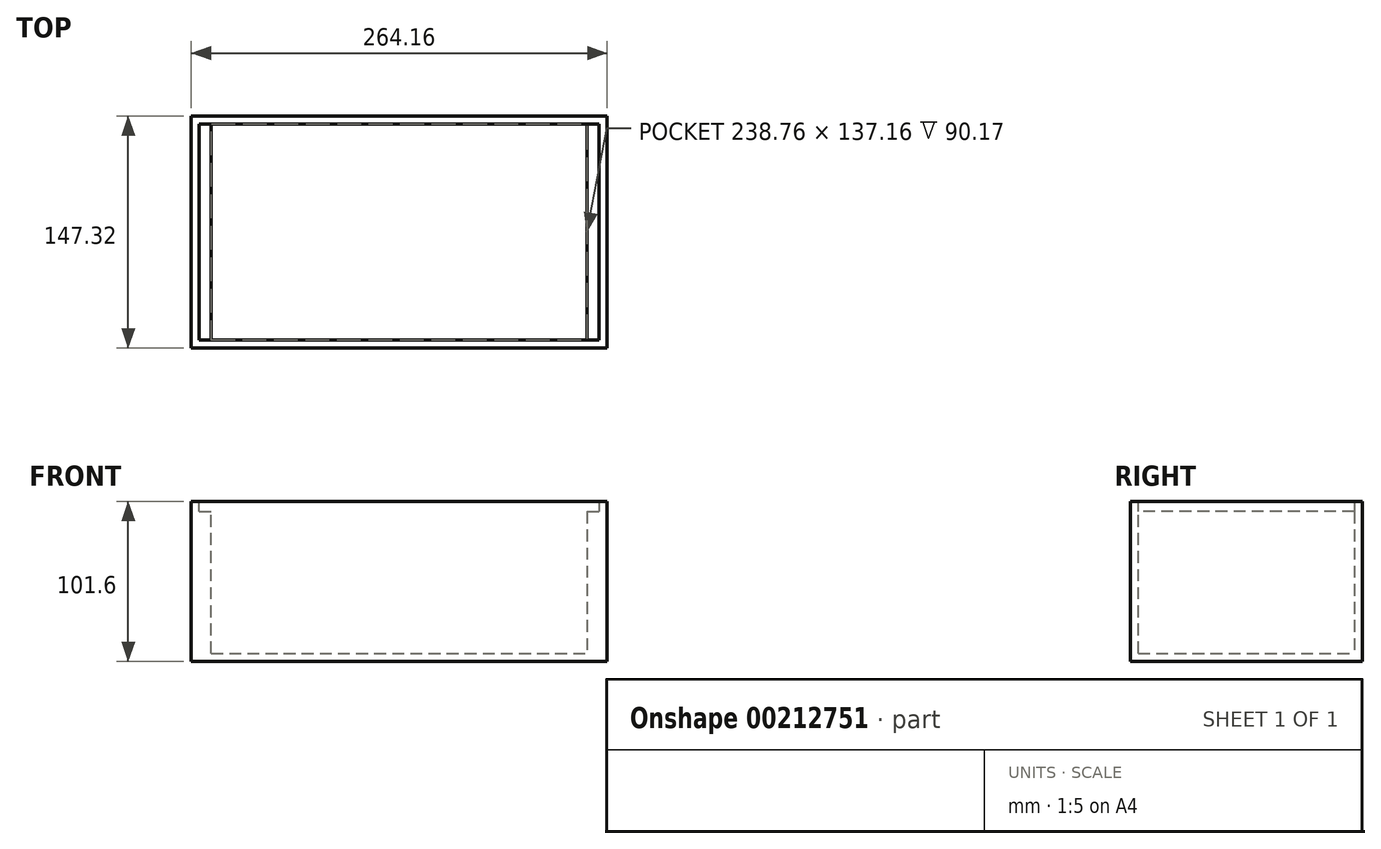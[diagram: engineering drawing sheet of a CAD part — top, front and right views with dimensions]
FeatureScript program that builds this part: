
annotation { "Feature Type Name" : "Feature", "Feature Type Description" : "" }
export const myFeature = defineFeature(function(context is Context, id is Id, definition is map)
    precondition{}
    {
        {
            var Q0;
            Q0=qCreatedBy(makeId("Top.planeOp"),FACE);
            var sketch = newSketch(context, id + "F0", { "sketchPlane" : qUnion([Q0])});
            skLineSegment(sketch, "E0.bottom", {"start": v(-132.08, 73.66) * mm, "end": v(132.08, 73.66) * mm});
            skLineSegment(sketch, "E0.top", {"start": v(-132.08, -73.66) * mm, "end": v(132.08, -73.66) * mm});
            skLineSegment(sketch, "E0.left", {"start": v(-132.08, 73.66) * mm, "end": v(-132.08, -73.66) * mm});
            skLineSegment(sketch, "E0.right", {"start": v(132.08, 73.66) * mm, "end": v(132.08, -73.66) * mm});
            skPoint(sketch, "E0.middle", {"position": v(0, 0) * mm});
            skSolve(sketch);
        }
        {
            var Q0;
            Q0=makeQuery(id+"F0.imprint","IMPRINT",FACE,{"disambiguationData":[TD([[makeQuery(id+"F0.imprint","IMPRINT",EDGE,{"derivedFrom":sQuery(id+"F0.wireOp",EDGE,"E0.bottom")}),-1.0]])]});
            extrude(context, id + "F1", {"entities" : qUnion([Q0]), "depth" : 5.08 * mm});
        }
        {
            var Q0;
            Q0=qCreatedBy(makeId("Right.planeOp"),FACE);
            cPlane(context, id + "F2", {"entities" : qUnion([Q0]), "cplaneType" : CPlaneType.OFFSET, "offset" : 132.08 * mm, "oppositeDirection" : true, "width" : 152.4 * mm, "height" : 152.4 * mm});
        }
        {
            var Q0;
            Q0=qCreatedBy(id+"F2.planeOp",FACE);
            var sketch = newSketch(context, id + "F3", { "sketchPlane" : qUnion([Q0])});
            skLineSegment(sketch, "E1", {"start": v(0, 0) * mm, "end": v(73.66, 0) * mm});
            skLineSegment(sketch, "E2", {"start": v(73.66, 0) * mm, "end": v(73.66, 95.25) * mm});
            skLineSegment(sketch, "E3", {"start": v(73.66, 95.25) * mm, "end": v(0, 95.25) * mm});
            skLineSegment(sketch, "E4.MirrorCS", {"start": v(-73.66, 95.25) * mm, "end": v(0, 95.25) * mm});
            skLineSegment(sketch, "E5.MirrorCS", {"start": v(-73.66, 0) * mm, "end": v(-73.66, 95.25) * mm});
            skLineSegment(sketch, "E6.MirrorCS", {"start": v(0, 0) * mm, "end": v(-73.66, 0) * mm});
            skSolve(sketch);
        }
        {
            var Q0;
            Q0=makeQuery(id+"F3.imprint","IMPRINT",FACE,{"disambiguationData":[TD([[makeQuery(id+"F3.imprint","IMPRINT",EDGE,{"derivedFrom":sQuery(id+"F3.wireOp",EDGE,"E1")}),1.0]])]});
            extrude(context, id + "F4", {"entities" : qUnion([Q0]), "depth" : 12.7 * mm});
        }
        {
            var Q0;
            Q0=qCreatedBy(makeId("Front.planeOp"),FACE);
            cPlane(context, id + "F5", {"entities" : qUnion([Q0]), "cplaneType" : CPlaneType.OFFSET, "offset" : 73.66 * mm, "width" : 152.4 * mm, "height" : 152.4 * mm});
        }
        {
            var Q0;
            Q0=qCreatedBy(id+"F5.planeOp",FACE);
            var sketch = newSketch(context, id + "F6", { "sketchPlane" : qUnion([Q0])});
            skLineSegment(sketch, "E7", {"start": v(0, 0) * mm, "end": v(-132.08, 0) * mm});
            skLineSegment(sketch, "E8", {"start": v(-132.08, 0) * mm, "end": v(-132.08, 101.6) * mm});
            skLineSegment(sketch, "E9", {"start": v(-132.08, 101.6) * mm, "end": v(132.08, 101.6) * mm});
            skLineSegment(sketch, "E10", {"start": v(132.08, 101.6) * mm, "end": v(132.08, 0) * mm});
            skLineSegment(sketch, "E11", {"start": v(132.08, 0) * mm, "end": v(0, 0) * mm});
            skSolve(sketch);
        }
        {
            var Q0;
            Q0=makeQuery(id+"F6.imprint","IMPRINT",FACE,{"disambiguationData":[TD([[makeQuery(id+"F6.imprint","IMPRINT",EDGE,{"derivedFrom":sQuery(id+"F6.wireOp",EDGE,"E7")}),-1.0]])]});
            extrude(context, id + "F7", {"entities" : qUnion([Q0]), "oppositeDirection" : true, "depth" : 5.08 * mm});
        }
        {
            var Q0;
            Q0=makeQuery(id+"F7.opExtrude","SWEPT_BODY",BODY,{"disambiguationData":[OSD([sQuery(id+"F6.wireOp",EDGE,"E7"),sQuery(id+"F6.wireOp",EDGE,"E8"),sQuery(id+"F6.wireOp",EDGE,"E9"),sQuery(id+"F6.wireOp",EDGE,"E10"),sQuery(id+"F6.wireOp",EDGE,"E11")])]});
            var Q1;
            Q1=qCreatedBy(makeId("Front.planeOp"),FACE);
            mirror(context, id + "F8", {"entities" : qUnion([Q0]), "mirrorPlane" : qUnion([Q1])});
        }
        {
            var Q0;
            Q0=qCreatedBy(makeId("Right.planeOp"),FACE);
            cPlane(context, id + "F9", {"entities" : qUnion([Q0]), "cplaneType" : CPlaneType.OFFSET, "offset" : 132.08 * mm, "oppositeDirection" : true, "width" : 152.4 * mm, "height" : 152.4 * mm});
        }
        {
            var Q0;
            Q0=qCreatedBy(id+"F9.planeOp",FACE);
            var sketch = newSketch(context, id + "F10", { "sketchPlane" : qUnion([Q0])});
            skLineSegment(sketch, "E12", {"start": v(-73.66, 101.6) * mm, "end": v(-73.66, 0) * mm});
            skLineSegment(sketch, "E13", {"start": v(73.66, 95.25) * mm, "end": v(73.66, 0) * mm});
            skLineSegment(sketch, "E14", {"start": v(0, 0) * mm, "end": v(73.66, 0) * mm});
            skLineSegment(sketch, "E15", {"start": v(0, 0) * mm, "end": v(-73.66, 0) * mm});
            skLineSegment(sketch, "E16", {"start": v(73.66, 95.25) * mm, "end": v(73.66, 101.6) * mm});
            skLineSegment(sketch, "E17", {"start": v(73.66, 101.6) * mm, "end": v(-73.66, 101.6) * mm});
            skLineSegment(sketch, "E18", {"start": v(73.66, 95.25) * mm, "end": v(-73.66, 95.25) * mm});
            skSolve(sketch);
        }
        {
            var Q0;
            Q0=makeQuery(id+"F10.imprint","IMPRINT",FACE,{"disambiguationData":[TD([[makeQuery(id+"F10.imprint","IMPRINT",EDGE,{"derivedFrom":sQuery(id+"F10.wireOp",EDGE,"E16")}),1.0]])]});
            extrude(context, id + "F11", {"entities" : qUnion([Q0]), "depth" : 5.08 * mm});
        }
        {
            var Q0;
            Q0=makeQuery(id+"F11.opExtrude","SWEPT_BODY",BODY,{"disambiguationData":[OSD([sQuery(id+"F10.wireOp",EDGE,"E12"),sQuery(id+"F10.wireOp",EDGE,"E16"),sQuery(id+"F10.wireOp",EDGE,"E17"),sQuery(id+"F10.wireOp",EDGE,"E18")])]});
            var Q1;
            Q1=makeQuery(id+"F4.opExtrude","SWEPT_BODY",BODY,{"disambiguationData":[OSD([sQuery(id+"F3.wireOp",EDGE,"E1"),sQuery(id+"F3.wireOp",EDGE,"E2"),sQuery(id+"F3.wireOp",EDGE,"E3"),sQuery(id+"F3.wireOp",EDGE,"E4.MirrorCS"),sQuery(id+"F3.wireOp",EDGE,"E5.MirrorCS"),sQuery(id+"F3.wireOp",EDGE,"E6.MirrorCS")])]});
            var Q2;
            Q2=qCreatedBy(makeId("Right.planeOp"),FACE);
            mirror(context, id + "F12", {"operationType" : NewBodyOperationType.ADD, "entities" : qUnion([Q0, Q1]), "mirrorPlane" : qUnion([Q2])});
        }
    });
